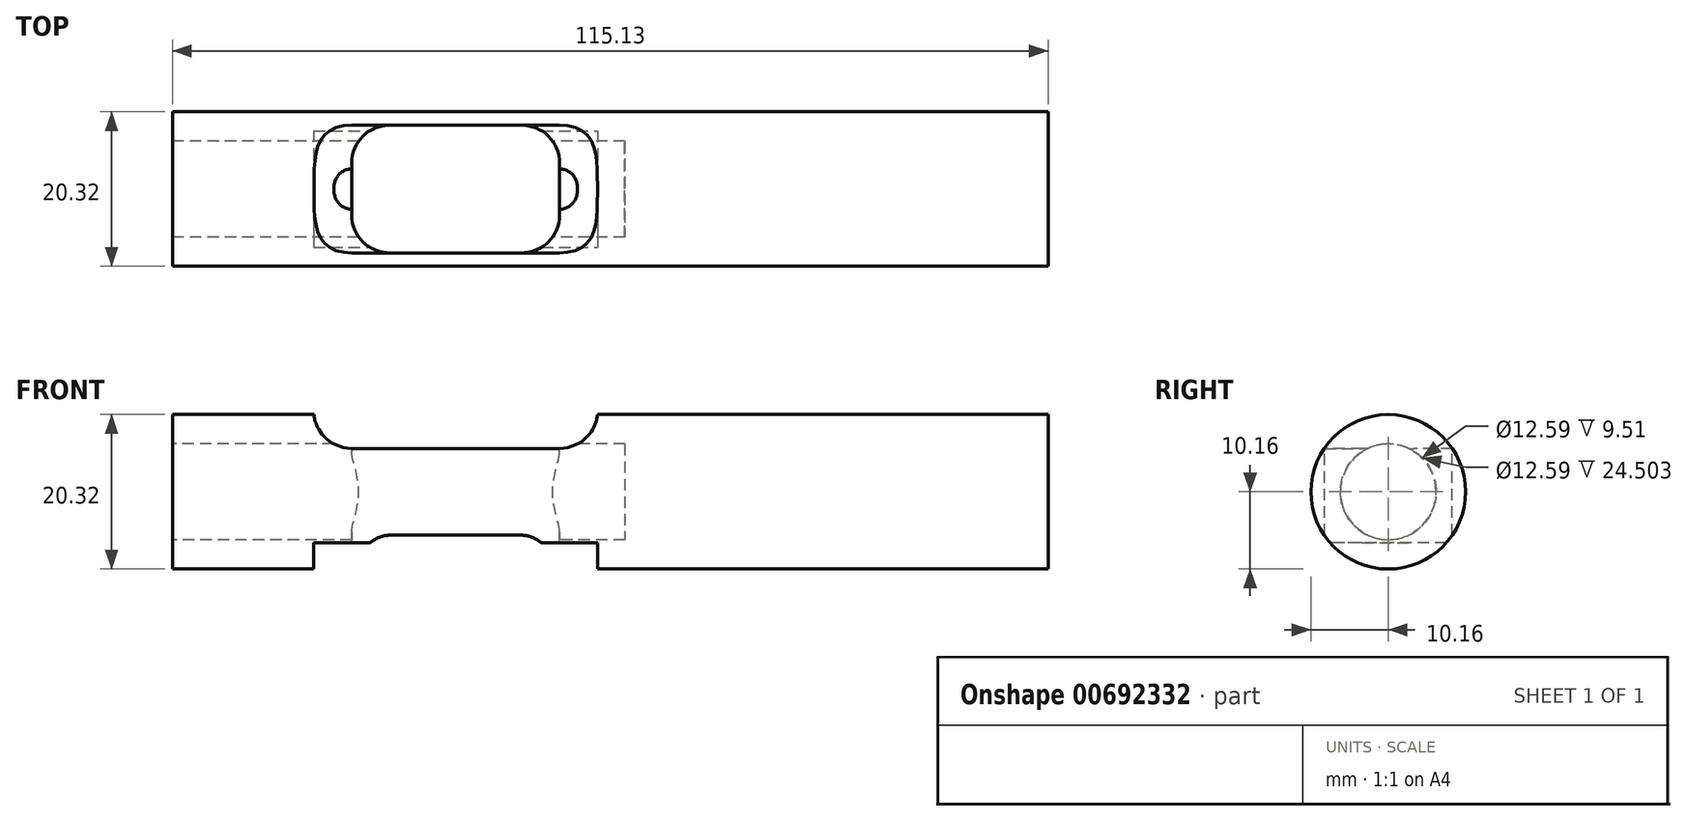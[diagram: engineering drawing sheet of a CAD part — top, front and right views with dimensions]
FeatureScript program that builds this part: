
annotation { "Feature Type Name" : "Feature", "Feature Type Description" : "" }
export const myFeature = defineFeature(function(context is Context, id is Id, definition is map)
    precondition{}
    {
        {
            var Q0;
            Q0=qCreatedBy(makeId("Front.planeOp"),FACE);
            var sketch = newSketch(context, id + "F0", { "sketchPlane" : qUnion([Q0])});
            skLineSegment(sketch, "E0", {"start": v(-59.11, 0) * mm, "end": v(-59.11, 10.16) * mm});
            skLineSegment(sketch, "E1", {"start": v(-59.11, 10.16) * mm, "end": v(56.02, 10.16) * mm});
            skLineSegment(sketch, "E2", {"start": v(56.02, 10.16) * mm, "end": v(56.02, 0) * mm});
            skLineSegment(sketch, "E3", {"start": v(56.02, 0) * mm, "end": v(-59.11, 0) * mm});
            skSolve(sketch);
        }
        {
            var Q0;
            Q0 = qSketchRegion(id + "F0", true);
            var Q1;
            Q1=sQuery(id+"F0.wireOp",EDGE,"E3");
            revolve(context, id + "F1", {"entities" : qUnion([Q0]), "axis" : qUnion([Q1]), "revolveType" : RevolveType.FULL});
        }
        {
            var Q0;
            Q0=qCreatedBy(makeId("Front.planeOp"),FACE);
            var sketch = newSketch(context, id + "F2", { "sketchPlane" : qUnion([Q0])});
            skLineSegment(sketch, "E4.bottom", {"start": v(-40.54, 19.64) * mm, "end": v(-3.2, 19.64) * mm});
            skLineSegment(sketch, "E4.top", {"start": v(-35.54, 5.7) * mm, "end": v(-8.2, 5.7) * mm});
            skLineSegment(sketch, "E4.left", {"start": v(-40.54, 19.64) * mm, "end": v(-40.54, 10.7) * mm});
            skLineSegment(sketch, "E4.right", {"start": v(-3.2, 19.64) * mm, "end": v(-3.2, 10.7) * mm});
            skPoint(sketch, "E5.visualSharp", {"position": v(-40.54, 5.7) * mm});
            skArc(sketch, "E5.filletArc", {"start": v(-40.54, 10.7) * mm, "mid": v(-39.07, 7.17) * mm, "end": v(-35.54, 5.7) * mm});
            skPoint(sketch, "E6.visualSharp", {"position": v(-3.2, 5.7) * mm});
            skArc(sketch, "E6.filletArc", {"start": v(-8.2, 5.7) * mm, "mid": v(-4.66, 7.17) * mm, "end": v(-3.2, 10.7) * mm});
            skLineSegment(sketch, "E7.bottom", {"start": v(-40.54, -6.68) * mm, "end": v(-3.2, -6.68) * mm});
            skLineSegment(sketch, "E7.top", {"start": v(-40.54, -19.06) * mm, "end": v(-3.2, -19.06) * mm});
            skLineSegment(sketch, "E7.left", {"start": v(-40.54, -6.68) * mm, "end": v(-40.54, -19.06) * mm});
            skLineSegment(sketch, "E7.right", {"start": v(-3.2, -6.68) * mm, "end": v(-3.2, -19.06) * mm});
            skSolve(sketch);
        }
        {
            var Q0;
            Q0 = qSketchRegion(id + "F2", true);
            extrude(context, id + "F3", {"entities" : qUnion([Q0]), "operationType" : NewBodyOperationType.REMOVE, "endBound" : BoundingType.SYMMETRIC, "oppositeDirection" : true, "depth" : 50 * mm, "offsetDistance" : 25 * mm});
        }
        {
            var Q0;
            Q0=makeQuery(id+"F1.opRevolve","SWEPT_FACE",FACE,{"disambiguationData":[OSD([sQuery(id+"F0.wireOp",EDGE,"E0")])]});
            var sketch = newSketch(context, id + "F4", { "sketchPlane" : qUnion([Q0])});
            skCircle(sketch, "E8", {"center": v(0, 0) * mm, "radius": 6.3 * mm});
            skSolve(sketch);
        }
        {
            var Q0;
            Q0 = qSketchRegion(id + "F4", true);
            extrude(context, id + "F5", {"entities" : qUnion([Q0]), "operationType" : NewBodyOperationType.REMOVE, "oppositeDirection" : true, "depth" : 59.5 * mm, "offsetDistance" : 25 * mm});
        }
        {
            var Q0;
            Q0=qCreatedBy(makeId("Top.planeOp"),FACE);
            var sketch = newSketch(context, id + "F6", { "sketchPlane" : qUnion([Q0])});
            skPoint(sketch, "E9.0.0.end.orphan", {"position": v(-8.2, -2.65) * mm});
            skPoint(sketch, "E10.0.2.start.orphan", {"position": v(-8.2, 2.65) * mm});
            skPoint(sketch, "E10.0.0.end.orphan", {"position": v(-35.54, 2.65) * mm});
            skPoint(sketch, "E9.0.2.start.orphan", {"position": v(-35.54, -2.65) * mm});
            skPoint(sketch, "E10.0.3.end.orphan", {"position": v(-35.54, 8.4) * mm});
            skPoint(sketch, "E10.0.3.start.orphan", {"position": v(-8.2, 8.4) * mm});
            skPoint(sketch, "E9.0.3.end.orphan", {"position": v(-35.54, -8.4) * mm});
            skPoint(sketch, "E9.0.3.start.orphan", {"position": v(-8.2, -8.4) * mm});
            skLineSegment(sketch, "E11.bottom", {"start": v(-30.54, 8.4) * mm, "end": v(-13.2, 8.4) * mm});
            skLineSegment(sketch, "E11.top", {"start": v(-30.54, -8.4) * mm, "end": v(-13.2, -8.4) * mm});
            skLineSegment(sketch, "E11.left", {"start": v(-35.54, 3.4) * mm, "end": v(-35.54, -3.4) * mm});
            skLineSegment(sketch, "E11.right", {"start": v(-8.2, 3.4) * mm, "end": v(-8.2, -3.4) * mm});
            skArc(sketch, "E12.filletArc", {"start": v(-30.54, 8.4) * mm, "mid": v(-34.07, 6.94) * mm, "end": v(-35.54, 3.4) * mm});
            skArc(sketch, "E13.filletArc", {"start": v(-35.54, -3.4) * mm, "mid": v(-34.07, -6.94) * mm, "end": v(-30.54, -8.4) * mm});
            skArc(sketch, "E14.filletArc", {"start": v(-13.2, -8.4) * mm, "mid": v(-9.66, -6.94) * mm, "end": v(-8.2, -3.4) * mm});
            skArc(sketch, "E15.filletArc", {"start": v(-8.2, 3.4) * mm, "mid": v(-9.66, 6.94) * mm, "end": v(-13.2, 8.4) * mm});
            skSolve(sketch);
        }
        {
            var Q0;
            Q0 = qSketchRegion(id + "F6", true);
            extrude(context, id + "F7", {"entities" : qUnion([Q0]), "operationType" : NewBodyOperationType.REMOVE, "endBound" : BoundingType.SYMMETRIC, "oppositeDirection" : true, "depth" : 50 * mm, "offsetDistance" : 25 * mm});
        }
    });
